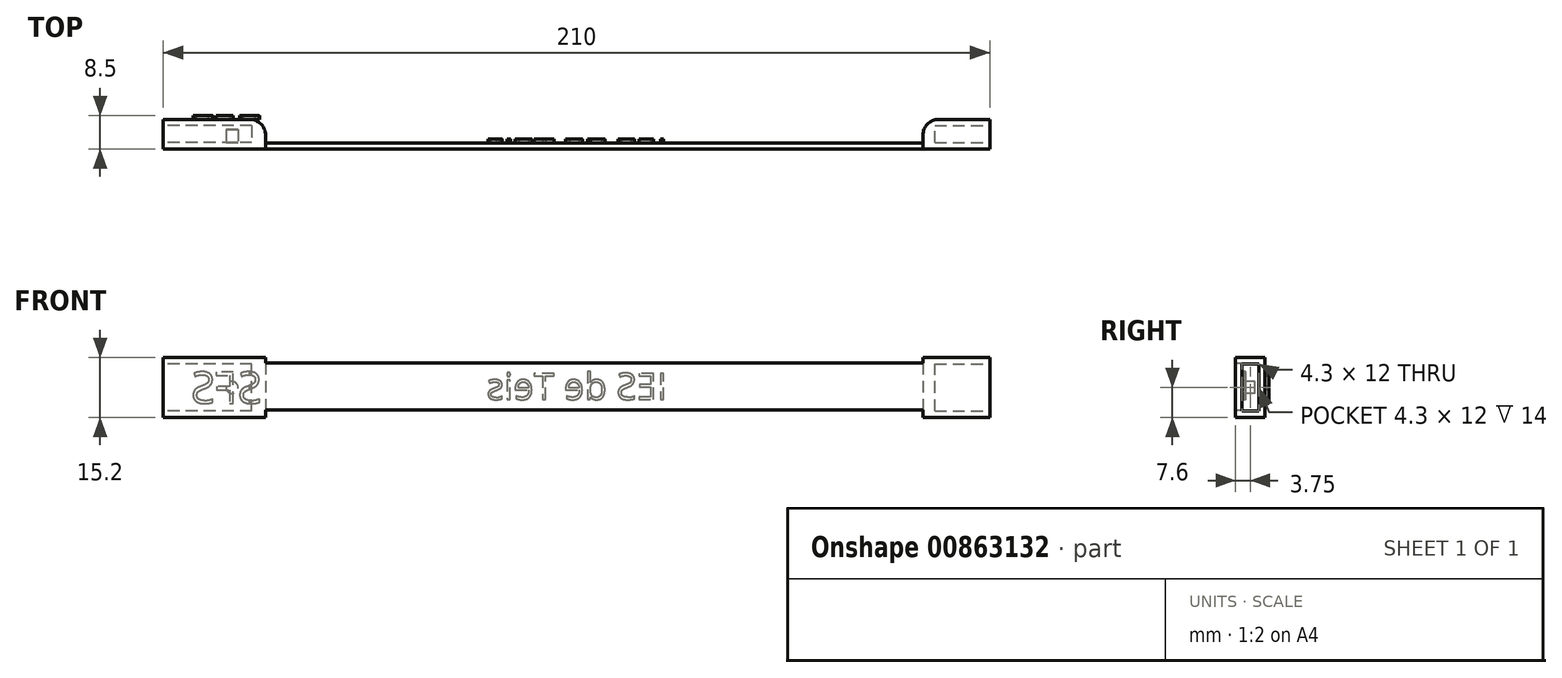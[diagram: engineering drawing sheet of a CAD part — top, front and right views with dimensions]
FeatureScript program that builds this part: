
annotation { "Feature Type Name" : "Feature", "Feature Type Description" : "" }
export const myFeature = defineFeature(function(context is Context, id is Id, definition is map)
    precondition{}
    {
        {
            var Q0;
            Q0=qCreatedBy(makeId("Front.planeOp"),FACE);
            var sketch = newSketch(context, id + "F0", { "sketchPlane" : qUnion([Q0])});
            skLineSegment(sketch, "E0.bottom", {"start": v(-100, -1.88) * mm, "end": v(100, -1.88) * mm});
            skLineSegment(sketch, "E0.top", {"start": v(-100, 10.12) * mm, "end": v(100, 10.12) * mm});
            skLineSegment(sketch, "E0.left", {"start": v(-100, -1.88) * mm, "end": v(-100, 10.12) * mm});
            skLineSegment(sketch, "E0.right", {"start": v(100, -1.87) * mm, "end": v(100, 10.12) * mm});
            skSolve(sketch);
        }
        {
            var Q0;
            Q0=qCreatedBy(makeId("Right.planeOp"),FACE);
            cPlane(context, id + "F1", {"entities" : qUnion([Q0]), "cplaneType" : CPlaneType.OFFSET, "offset" : 105 * mm, "width" : 150 * mm, "height" : 150 * mm});
        }
        {
            var Q0;
            Q0=qCreatedBy(makeId("Right.planeOp"),FACE);
            cPlane(context, id + "F2", {"entities" : qUnion([Q0]), "cplaneType" : CPlaneType.OFFSET, "offset" : 105 * mm, "oppositeDirection" : true, "width" : 150 * mm, "height" : 150 * mm});
        }
        {
            var Q0;
            Q0=qCreatedBy(id+"F1.planeOp",FACE);
            var sketch = newSketch(context, id + "F3", { "sketchPlane" : qUnion([Q0])});
            skLineSegment(sketch, "E1.bottom", {"start": v(0, -3.75) * mm, "end": v(7.5, -3.75) * mm});
            skLineSegment(sketch, "E1.top", {"start": v(0, 11.45) * mm, "end": v(7.5, 11.45) * mm});
            skLineSegment(sketch, "E1.left", {"start": v(0, -3.75) * mm, "end": v(0, 11.45) * mm});
            skLineSegment(sketch, "E1.right", {"start": v(7.5, -3.75) * mm, "end": v(7.5, 11.45) * mm});
            skSolve(sketch);
        }
        {
            var Q0;
            Q0=qCreatedBy(id+"F2.planeOp",FACE);
            var sketch = newSketch(context, id + "F4", { "sketchPlane" : qUnion([Q0])});
            skLineSegment(sketch, "E2.bottom", {"start": v(7.5, -3.75) * mm, "end": v(0, -3.75) * mm});
            skLineSegment(sketch, "E2.top", {"start": v(7.5, 11.45) * mm, "end": v(0, 11.45) * mm});
            skLineSegment(sketch, "E2.left", {"start": v(7.5, -3.75) * mm, "end": v(7.5, 11.45) * mm});
            skLineSegment(sketch, "E2.right", {"start": v(0, -3.75) * mm, "end": v(0, 11.45) * mm});
            skSolve(sketch);
        }
        {
            var Q0;
            Q0=makeQuery(id+"F3.imprint","IMPRINT",FACE,{"disambiguationData":[TD([[makeQuery(id+"F3.imprint","IMPRINT",EDGE,{"derivedFrom":sQuery(id+"F3.wireOp",EDGE,"E1.bottom")}),1.0]])]});
            var Q1;
            Q1=makeQuery(id+"F3.imprint","IMPRINT",FACE,{"disambiguationData":[TD([[makeQuery(id+"F3.imprint","IMPRINT",EDGE,{"derivedFrom":sQuery(id+"F3.wireOp",EDGE,"ULmGsHiY-Mv4B-d8Jg-noec-36pXMbrnfk32.bottom")}),1.0]])]});
            extrude(context, id + "F5", {"entities" : qUnion([Q0, Q1]), "oppositeDirection" : true, "depth" : 17 * mm, "offsetDistance" : 25 * mm});
        }
        {
            var Q0;
            Q0=qSketchRegion(id+"F4",true);
            var Q1;
            Q1=makeQuery(id+"F4.imprint","IMPRINT",FACE,{"disambiguationData":[TD([[makeQuery(id+"F4.imprint","IMPRINT",EDGE,{"derivedFrom":sQuery(id+"F4.wireOp",EDGE,"Hlka1Qad-GjJF-81ZI-ByxS-eIRTQnkwmmPv.bottom")}),1.0]])]});
            extrude(context, id + "F6", {"entities" : qUnion([Q0, Q1]), "depth" : 26 * mm, "offsetDistance" : 25 * mm});
        }
        {
            var Q0;
            Q0=qSketchRegion(id+"F0",true);
            extrude(context, id + "F7", {"entities" : qUnion([Q0]), "oppositeDirection" : true, "depth" : 1.5 * mm, "offsetDistance" : 25 * mm});
        }
        {
            var Q0;
            Q0=qCreatedBy(id+"F1.planeOp",FACE);
            var sketch = newSketch(context, id + "F8", { "sketchPlane" : qUnion([Q0])});
            skLineSegment(sketch, "E3.bottom", {"start": v(1.6, -2.15) * mm, "end": v(5.9, -2.15) * mm});
            skLineSegment(sketch, "E3.top", {"start": v(1.6, 9.85) * mm, "end": v(5.9, 9.85) * mm});
            skLineSegment(sketch, "E3.left", {"start": v(1.6, -2.15) * mm, "end": v(1.6, 9.85) * mm});
            skLineSegment(sketch, "E3.right", {"start": v(5.9, -2.15) * mm, "end": v(5.9, 9.85) * mm});
            skSolve(sketch);
        }
        {
            var Q0;
            Q0=qSketchRegion(id+"F8",true);
            extrude(context, id + "F9", {"entities" : qUnion([Q0]), "operationType" : NewBodyOperationType.REMOVE, "oppositeDirection" : true, "depth" : 14 * mm, "offsetDistance" : 25 * mm});
        }
        {
            var Q0;
            Q0=qCreatedBy(id+"F2.planeOp",FACE);
            var sketch = newSketch(context, id + "F10", { "sketchPlane" : qUnion([Q0])});
            skLineSegment(sketch, "E4.bottom", {"start": v(5.9, -2.15) * mm, "end": v(1.6, -2.15) * mm});
            skLineSegment(sketch, "E4.top", {"start": v(5.9, 9.85) * mm, "end": v(1.6, 9.85) * mm});
            skLineSegment(sketch, "E4.left", {"start": v(5.9, -2.15) * mm, "end": v(5.9, 9.85) * mm});
            skLineSegment(sketch, "E4.right", {"start": v(1.6, -2.15) * mm, "end": v(1.6, 9.85) * mm});
            skSolve(sketch);
        }
        {
            var Q0;
            Q0=qSketchRegion(id+"F10",true);
            extrude(context, id + "F11", {"entities" : qUnion([Q0]), "operationType" : NewBodyOperationType.REMOVE, "depth" : 22.5 * mm, "offsetDistance" : 25 * mm});
        }
        {
            var Q0;
            Q0=makeQuery(id+"F7.opExtrude","CAP_FACE",FACE,{"disambiguationData":[OSD([sQuery(id+"F0.wireOp",EDGE,"E0.bottom"),sQuery(id+"F0.wireOp",EDGE,"E0.top"),sQuery(id+"F0.wireOp",EDGE,"E0.left"),sQuery(id+"F0.wireOp",EDGE,"E0.right")])],"isStart":false});
            var sketch = newSketch(context, id + "F12", { "sketchPlane" : qUnion([Q0])});
            skText(sketch, "E5", { "text": "IES de Teis", "fontName": "OpenSans-Regular.ttf"});
            const initialGuessF12  = {"E5": [-0.02305, 0.0008, 1, 0, 0.00672]};
            skSetInitialGuess(sketch, initialGuessF12);
            skSolve(sketch);
        }
        {
            var Q0;
            Q0=qSketchRegion(id+"F12",true);
            extrude(context, id + "F13", {"entities" : qUnion([Q0]), "operationType" : NewBodyOperationType.ADD, "depth" : 1 * mm, "offsetDistance" : 25 * mm});
        }
        {
            var Q0;
            Q0=makeQuery(id+"F6.opExtrude","CAP_EDGE",EDGE,{"disambiguationData":[OSD([sQuery(id+"F4.wireOp",EDGE,"E2.left")])],"isStart":false});
            var Q1;
            Q1=makeQuery(id+"F5.opExtrude","CAP_EDGE",EDGE,{"disambiguationData":[OSD([sQuery(id+"F3.wireOp",EDGE,"E1.right")])],"isStart":false});
            fillet(context, id + "F14", {"entities" : qUnion([Q0, Q1]), "radius" : 4 * mm, "tangentPropagation" : true, "allowEdgeOverflow" : false});
        }
        {
            var Q0;
            Q0=makeQuery(id+"F5.opExtrude","SWEPT_BODY",BODY,{"disambiguationData":[OSD([sQuery(id+"F3.wireOp",EDGE,"E1.bottom"),sQuery(id+"F3.wireOp",EDGE,"E1.top"),sQuery(id+"F3.wireOp",EDGE,"E1.left"),sQuery(id+"F3.wireOp",EDGE,"E1.right")])]});
            var Q1;
            Q1=makeQuery(id+"F6.opExtrude","SWEPT_BODY",BODY,{"disambiguationData":[OSD([sQuery(id+"F4.wireOp",EDGE,"E2.bottom"),sQuery(id+"F4.wireOp",EDGE,"E2.top"),sQuery(id+"F4.wireOp",EDGE,"E2.left"),sQuery(id+"F4.wireOp",EDGE,"E2.right")])]});
            var Q2;
            Q2=makeQuery(id+"F7.opExtrude","SWEPT_BODY",BODY,{"disambiguationData":[OSD([sQuery(id+"F0.wireOp",EDGE,"E0.bottom"),sQuery(id+"F0.wireOp",EDGE,"E0.top"),sQuery(id+"F0.wireOp",EDGE,"E0.left"),sQuery(id+"F0.wireOp",EDGE,"E0.right")])]});
            booleanBodies(context, id + "F15", {"operationType" : BooleanOperationType.UNION, "tools" : qUnion([Q0, Q1, Q2])});
        }
        {
            var Q0;
            Q0=makeQuery(id+"F6.opExtrude","SWEPT_FACE",FACE,{"disambiguationData":[OSD([sQuery(id+"F4.wireOp",EDGE,"E2.left")])]});
            var sketch = newSketch(context, id + "F16", { "sketchPlane" : qUnion([Q0])});
            skText(sketch, "E6", { "text": "SFS", "fontName": "OpenSans-Regular.ttf"});
            const initialGuessF16  = {"E6": [0.08, -0.00015, 1, 5e-05, 0.008]};
            skSetInitialGuess(sketch, initialGuessF16);
            skSolve(sketch);
        }
        {
            var Q0;
            Q0=qSketchRegion(id+"F16",true);
            extrude(context, id + "F17", {"entities" : qUnion([Q0]), "operationType" : NewBodyOperationType.ADD, "depth" : 1 * mm, "offsetDistance" : 25 * mm});
        }
        {
            var Q0;
            Q0=makeQuery(id+"F15.opBoolean","MERGE",FACE,{"derivedFrom":[makeQuery(id+"F5.opExtrude","SWEPT_FACE",FACE,{"disambiguationData":[OSD([sQuery(id+"F3.wireOp",EDGE,"E1.left")])]}),makeQuery(id+"F6.opExtrude","SWEPT_FACE",FACE,{"disambiguationData":[OSD([sQuery(id+"F4.wireOp",EDGE,"E2.right")])]}),makeQuery(id+"F7.opExtrude","CAP_FACE",FACE,{"disambiguationData":[OSD([sQuery(id+"F0.wireOp",EDGE,"E0.bottom"),sQuery(id+"F0.wireOp",EDGE,"E0.top"),sQuery(id+"F0.wireOp",EDGE,"E0.left"),sQuery(id+"F0.wireOp",EDGE,"E0.right")])],"isStart":true})]});
            var sketch = newSketch(context, id + "F18", { "sketchPlane" : qUnion([Q0])});
            skPoint(sketch, "E7", {"position": v(-87.5, 3.85) * mm});
            skPoint(sketch, "E7.positionSnap0", {"position": v(-105, 3.85) * mm});
            skCircle(sketch, "E8", {"center": v(-87.5, 3.85) * mm, "radius": 1.5 * mm});
            skSolve(sketch);
        }
        {
            var Q0;
            Q0=makeQuery(id+"F18.imprint","IMPRINT",FACE,{"disambiguationData":[TD([[makeQuery(id+"F18.imprint","IMPRINT",EDGE,{"derivedFrom":sQuery(id+"F18.wireOp",EDGE,"E8")}),1.0]])]});
            extrude(context, id + "F19", {"entities" : qUnion([Q0]), "operationType" : NewBodyOperationType.ADD, "oppositeDirection" : true, "depth" : 5 * mm, "offsetDistance" : 25 * mm});
        }
    });
